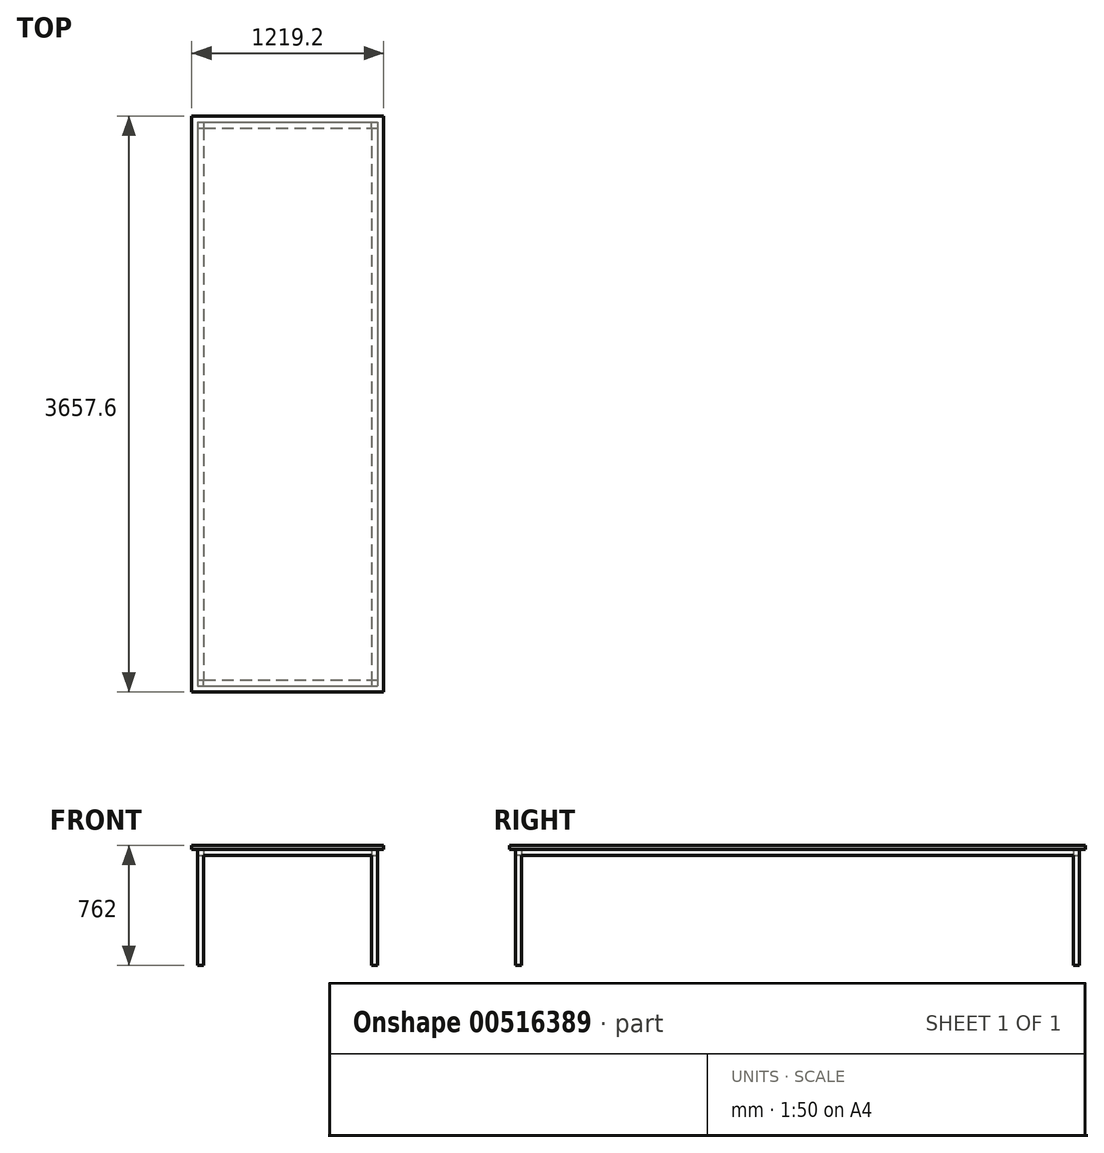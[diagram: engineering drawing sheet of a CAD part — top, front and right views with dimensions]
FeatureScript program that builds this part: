
annotation { "Feature Type Name" : "Feature", "Feature Type Description" : "" }
export const myFeature = defineFeature(function(context is Context, id is Id, definition is map)
    precondition{}
    {
        {
            var Q0;
            Q0=qCreatedBy(makeId("Top.planeOp"),FACE);
            var sketch = newSketch(context, id + "F0", { "sketchPlane" : qUnion([Q0])});
            skLineSegment(sketch, "E0.bottom", {"start": v(-571.5, 1790.7) * mm, "end": v(571.5, 1790.7) * mm});
            skLineSegment(sketch, "E0.top", {"start": v(-571.5, -1790.7) * mm, "end": v(571.5, -1790.7) * mm});
            skLineSegment(sketch, "E0.left", {"start": v(-571.5, 1790.7) * mm, "end": v(-571.5, -1790.7) * mm});
            skLineSegment(sketch, "E0.right", {"start": v(571.5, 1790.7) * mm, "end": v(571.5, -1790.7) * mm});
            skLineSegment(sketch, "E1.bottom", {"start": v(-571.5, -1790.7) * mm, "end": v(-571.5, -1790.7) * mm});
            skLineSegment(sketch, "E1.top", {"start": v(-571.5, 1790.7) * mm, "end": v(-571.5, 1790.7) * mm});
            skLineSegment(sketch, "E1.left", {"start": v(-571.5, -1790.7) * mm, "end": v(-571.5, 1790.7) * mm});
            skLineSegment(sketch, "E1.right", {"start": v(-571.5, -1790.7) * mm, "end": v(-571.5, 1790.7) * mm});
            skLineSegment(sketch, "E2.bottom", {"start": v(-533.4, 1752.6) * mm, "end": v(533.4, 1752.6) * mm});
            skLineSegment(sketch, "E2.top", {"start": v(-533.4, -1752.6) * mm, "end": v(533.4, -1752.6) * mm});
            skLineSegment(sketch, "E2.left", {"start": v(-533.4, 1752.6) * mm, "end": v(-533.4, -1752.6) * mm});
            skLineSegment(sketch, "E2.right", {"start": v(533.4, 1752.6) * mm, "end": v(533.4, -1752.6) * mm});
            skSolve(sketch);
        }
        {
            var Q0;
            Q0 = qSketchRegion(id + "F0", true);
            extrude(context, id + "F1", {"entities" : qUnion([Q0]), "depth" : 38.1 * mm, "offsetDistance" : 25.4 * mm});
        }
        {
            var Q0;
            Q0=makeQuery(id+"F1.opExtrude","CAP_FACE",FACE,{"disambiguationData":[OSD([sQuery(id+"F0.wireOp",EDGE,"E0.bottom"),sQuery(id+"F0.wireOp",EDGE,"E0.top"),sQuery(id+"F0.wireOp",EDGE,"E0.right"),sQuery(id+"F0.wireOp",EDGE,"E1.right"),sQuery(id+"F0.wireOp",EDGE,"E2.bottom"),sQuery(id+"F0.wireOp",EDGE,"E2.top"),sQuery(id+"F0.wireOp",EDGE,"E2.left"),sQuery(id+"F0.wireOp",EDGE,"E2.right")])],"isStart":true});
            var sketch = newSketch(context, id + "F2", { "sketchPlane" : qUnion([Q0])});
            skLineSegment(sketch, "E3.bottom", {"start": v(-571.5, 1790.7) * mm, "end": v(-533.4, 1790.7) * mm});
            skLineSegment(sketch, "E3.top", {"start": v(-571.5, 1752.6) * mm, "end": v(-533.4, 1752.6) * mm});
            skLineSegment(sketch, "E3.left", {"start": v(-571.5, 1790.7) * mm, "end": v(-571.5, 1752.6) * mm});
            skLineSegment(sketch, "E3.right", {"start": v(-533.4, 1790.7) * mm, "end": v(-533.4, 1752.6) * mm});
            skLineSegment(sketch, "E4.bottom", {"start": v(533.4, 1752.6) * mm, "end": v(571.5, 1752.6) * mm});
            skLineSegment(sketch, "E4.top", {"start": v(533.4, 1790.7) * mm, "end": v(571.5, 1790.7) * mm});
            skLineSegment(sketch, "E4.left", {"start": v(533.4, 1752.6) * mm, "end": v(533.4, 1790.7) * mm});
            skLineSegment(sketch, "E4.right", {"start": v(571.5, 1752.6) * mm, "end": v(571.5, 1790.7) * mm});
            skLineSegment(sketch, "E5.MirrorCS", {"start": v(-533.4, -1790.7) * mm, "end": v(-533.4, -1752.6) * mm});
            skLineSegment(sketch, "E6.MirrorCS", {"start": v(-571.5, -1790.7) * mm, "end": v(-533.4, -1790.7) * mm});
            skLineSegment(sketch, "E7.MirrorCS", {"start": v(-571.5, -1790.7) * mm, "end": v(-571.5, -1752.6) * mm});
            skLineSegment(sketch, "E8.MirrorCS", {"start": v(-571.5, -1752.6) * mm, "end": v(-533.4, -1752.6) * mm});
            skLineSegment(sketch, "E9.MirrorCS", {"start": v(533.4, -1752.6) * mm, "end": v(571.5, -1752.6) * mm});
            skLineSegment(sketch, "E10.MirrorCS", {"start": v(533.4, -1752.6) * mm, "end": v(533.4, -1790.7) * mm});
            skLineSegment(sketch, "E11.MirrorCS", {"start": v(533.4, -1790.7) * mm, "end": v(571.5, -1790.7) * mm});
            skLineSegment(sketch, "E12.MirrorCS", {"start": v(571.5, -1752.6) * mm, "end": v(571.5, -1790.7) * mm});
            skSolve(sketch);
        }
        {
            var Q0;
            Q0 = qSketchRegion(id + "F2", true);
            extrude(context, id + "F3", {"entities" : qUnion([Q0]), "operationType" : NewBodyOperationType.ADD, "depth" : 698.5 * mm, "offsetDistance" : 25.4 * mm});
        }
        {
            var Q0;
            Q0=makeQuery(id+"F1.opExtrude","CAP_FACE",FACE,{"disambiguationData":[OSD([sQuery(id+"F0.wireOp",EDGE,"E0.bottom"),sQuery(id+"F0.wireOp",EDGE,"E0.top"),sQuery(id+"F0.wireOp",EDGE,"E0.right"),sQuery(id+"F0.wireOp",EDGE,"E1.right"),sQuery(id+"F0.wireOp",EDGE,"E2.bottom"),sQuery(id+"F0.wireOp",EDGE,"E2.top"),sQuery(id+"F0.wireOp",EDGE,"E2.left"),sQuery(id+"F0.wireOp",EDGE,"E2.right")])],"isStart":false});
            var sketch = newSketch(context, id + "F4", { "sketchPlane" : qUnion([Q0])});
            skLineSegment(sketch, "E13.bottom", {"start": v(-609.6, 1828.8) * mm, "end": v(609.6, 1828.8) * mm});
            skLineSegment(sketch, "E13.top", {"start": v(-609.6, -1828.8) * mm, "end": v(609.6, -1828.8) * mm});
            skLineSegment(sketch, "E13.left", {"start": v(-609.6, 1828.8) * mm, "end": v(-609.6, -1828.8) * mm});
            skLineSegment(sketch, "E13.right", {"start": v(609.6, 1828.8) * mm, "end": v(609.6, -1828.8) * mm});
            skSolve(sketch);
        }
        {
            var Q0;
            Q0 = qSketchRegion(id + "F4", true);
            extrude(context, id + "F5", {"entities" : qUnion([Q0]), "operationType" : NewBodyOperationType.ADD, "depth" : 25.4 * mm, "offsetDistance" : 25.4 * mm});
        }
    });
